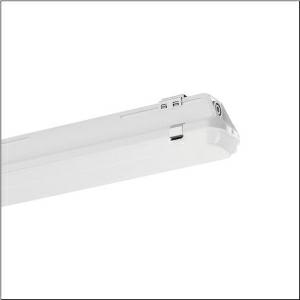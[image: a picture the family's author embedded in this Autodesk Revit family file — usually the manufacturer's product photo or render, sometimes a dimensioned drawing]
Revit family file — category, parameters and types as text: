
# Revit family: monsun_r__12_emergency_51fp107p467h3g_c051
name_source: partatom
category: Lighting Fixtures
units: mm (PartAtom-declared; Revit-internal decimal feet)

## family parameters
Cut with Voids When Loaded = No
Host = Face
Light Source = No
Part Type = Normal
Room Calculation Point = No
Round Connector Dimension = Use Diameter
Shared = No

## types (1)
- Monsun® 12 emergency (1 x LED, 6050 lm, 37.2 W, 4000K)
    Apparent Load = 37 VA
    CIE Flux Codes = 47 77 93 94 100
    Color Rendering = 80
    Color Temperature = 4000K
    Default Elevation = 1800 mm
    Description = Monsun® 12 emergency, damp-proof luminaire, chain hanger, primary optical cover: enclosure, of PMMA, light emission: direct distribution, primary light characteristic: symmetric, installation type: suspended mounting, surface-mounted, horizontal mounting, vertical mounting, LED rated luminous flux: 6.050 lm, light colour: 840, colour temperature: 4000K, control gear: ECG, with terminal, 4-pole, max. 2.5mm², mains connection: 220..240V, AC, 50/60Hz, rated input power: 37W, control gear: single battery element, battery: NiCd, 4,5 Ah, mains connection: 230V, 50Hz, luminaire housing, of glass-fibre reinforced polyester, uncoated, bright grey, length: 1.590 mm, width: 90 mm, height: 88mm, clip for enclosure, of stainless steel (V2A), ceiling mounting element, of stainless steel (V2A), chain hanger, of stainless steel (V2A), protection rating (complete): IP66, insulation class (complete): insulation class I (protective earthing), certification: CE, protection symbol: D, impact resistance: IK04, permissible ambient temperature for indoor applications: +5..+35°C, standard: EN 50419, EN 60598-2-1, EN 60598-2-22, no direct snow, no direct sun, no direct rain, for indoor or canopied outdoor use, corresponds to IFS (International Featured Standards) requirements for safety and quality in the food industry, packaging unit: 1 piece
    Height = 89 mm
    Lamp = 1 x LED
    Lamp Light Flux = 6050 lm
    Lamp Power = 37.2 W
    Lamp count = 1
    Length = 1590 mm
    Luminous efficacy = 163 lm/W
    Manufacturer = Siteco
    ModVariant = No
    Model = 51FP107P467H3G
    Mounting Place = Ceiling
    Mounting Type = Pendant
    Number of Poles = 1
    OnlyDefault = Yes
    Power Factor = 1
    Product Name = Monsun® 12 emergency
    Product group = damp-proof luminaire | ceiling pendant
    ProductGroupID = 908
    Protection Class = Protection class I
    Protection Degree = IP 66
    RLX_Detail_Level = 1
    RlxData = <blob elided: 88649 chars, md5=4615c817>
    Socket = socket
    Standby Power = 0 W
    System Light Flux = 6050 lm
    System Power = 37 W
    Type Comments = Product without accessories
    Type Image = l_1004748.jpg
    URL = http://relux.com
    VarID = ---
    Voltage = 0 V
    Weight = 0.00 kg
    Width = 90 mm

## geometry (parser evidence)
native form markers: Blend x4, Sweep x13
no freeform markers — native parametric forms only
